# Revit family: HerzCon-узел прямого подключения для фанкойлов 120мм
name_source: partatom
category: Rohrzubehör
units: mm (PartAtom-declared; Revit-internal decimal feet)

## family parameters
Arbeitsebenenbasiert = Nein
Beim Laden mit Abzugskörper schneiden = Nein
Bemaßung runder Anschluss = Durchmesser verwenden
Gemeinsam genutzt = Nein
Immer vertikal = Ja
OmniClass-Nummer = 23.65.55.14
OmniClass-Titel = Valves for Liquid Services
Teiletyp = Unterbricht

## types (1)
- DN32
    D01 = 15 mm  [stored 0.0492126 ft]
    D02 = 33 mm  [stored 0.108268 ft]
    D03 = 24.5 mm  [stored 0.0803806 ft]
    D04 = 20 mm  [stored 0.0656168 ft]
    D05 = 54.5 mm  [stored 0.178806 ft]
    D06 = 45 mm  [stored 0.147638 ft]
    D07 = 39 mm  [stored 0.127953 ft]
    D08 = 18.4 mm  [stored 0.0603675 ft]
    D09 = 13 mm
    D10 = 21.4 mm  [stored 0.07021 ft]
    H01 = 34 mm
    Hersteller = HERZ Armaturen Ges.m.b.H.
    KD01 = 25 mm  [stored 0.082021 ft]
    KD02 = 20 mm  [stored 0.0656168 ft]
    KD03 = 20 mm  [stored 0.0656168 ft]
    KD04 = 13.9 mm  [stored 0.0456037 ft]
    KD05 = 12.5 mm  [stored 0.0410105 ft]
    KD06 = 15 mm  [stored 0.0492126 ft]
    KD07 = 23.3 mm
    KD08 = 24.5 mm  [stored 0.0803806 ft]
    KD09 = 11.25 mm  [stored 0.0369094 ft]
    KH01 = 33.5 mm  [stored 0.109908 ft]
    KH02 = 58.5 mm  [stored 0.191929 ft]
    KH03 = 66 mm  [stored 0.216535 ft]
    KL01 = 114 mm  [stored 0.374016 ft]
    KL02 = 16 mm  [stored 0.0524934 ft]
    KL03 = 57 mm  [stored 0.187008 ft]
    KL04 = 12 mm  [stored 0.0393701 ft]
    KL05 = 15.4 mm
    KL06 = 48.9 mm  [stored 0.160433 ft]
    KL07 = 21.8 mm  [stored 0.0715223 ft]
    KL08 = 70.7 mm  [stored 0.231955 ft]
    KL09 = 4.7 mm  [stored 0.0154199 ft]
    KR01 = 35 mm  [stored 0.114829 ft]
    KR02 = 18.25 mm  [stored 0.0598753 ft]
    L01 = 15 mm  [stored 0.0492126 ft]
    L02 = 6.1 mm  [stored 0.0200131 ft]
    L03 = 22.4 mm  [stored 0.0734908 ft]
    L04 = 55 mm  [stored 0.180446 ft]
    L05 = 26.5 mm  [stored 0.0869423 ft]
    L06 = 17 mm
    L07 = 19.25 mm  [stored 0.0631562 ft]
    L08 = 14.75 mm
    L09 = 20 mm  [stored 0.0656168 ft]
    L10 = 29.3 mm  [stored 0.0961286 ft]
    L11 = 16 mm  [stored 0.0524934 ft]
    SCRNCODE = 05;04;04
    SCRNSEQ = ARM;TYP_ARM="DURR";02
    URL = www.herz-armaturen.ru
    kvs-Wert (обычная работа) = 4.57
    kvs-Wert (работа байпаса) = 14.2
    Корпус = латунь, устойчивая к селективной цинковой коррозии
    Макс. дифференциальное давление = 400000.0 Pa
    Макс. рабочая температура = 130 °C
    Макс. рабочее давление = 2500000.0 Pa
    Мембрана и уплотнительное кольцо O-Ring = EPDM
    Мин. рабочая температура = -20 °C
    Применение = HerzCON был разработан для простого подключения фанкойлов или AHU.
HerzCON - это устройство, состоящее из независимого от давления комби-клапана - регулятора расхода (4006), HERZ фильтра-грязевика, HERZ крана для слива (2512) и двух HERZ мультифункциональных шаровых кранов.
Включение, выключение и модульное управление возможно производить через приводы 0 - 10 В.
Приводы могут быть интегрированы в BMS при необходимости.
Устройство обеспечивает независимое от давления управление и в то же время гарантирует постоянный расход для конечного потребителя, максимизируя энергоэффективность системы.
Устройство HerzCON также позволяет производить промывку и запирание.
HerzCON предназначен для работы как в системах холодоснабжения, так и теплоснабжения.
Кран для слива, установленный на сетчатом фильтре, позволяет производить промывку устройства без необходимости извлечения сетчатого фильтра, а также позволяет очищать сетчатый фильтр в самом устройстве.
    Среда = Вода для системы отопления подготавливается в соответствии с ÖNORM H5195 или VDI 2035.
Возможно использование этилена или пропиленгликоля в концентрации 25-50% объема.
    Ход = 4 мм

note: [stored X ft] marks values corroborated as IEEE doubles in the binary element streams (Revit-internal decimal feet)
